FCSTD DOCUMENT  (FreeCAD 0.20R29603 (Git))
Label: equations_for_path_planning
License: All rights reserved
LicenseURL: http://en.wikipedia.org/wiki/All_rights_reserved
objects: Sketcher::SketchObject×12, PartDesign::Body×1, Spreadsheet::Sheet×1
note: 13 computed .brp shape members not serialized (recipe doc carries the construction recipe); baked Part::Feature solids carry a one-line shape summary decoded from their .brp

FEATURE [Sketcher::SketchObject] Sketch
  FullyConstrained = false
  MapMode = 5
  Support = -> [XY_Plane]
  sketch-geometry (40):
    g0: LineSegment StartX=13.0972 StartY=-137.963 StartZ=0 EndX=-119.149 EndY=-55.8265 EndZ=0
    g1: LineSegment StartX=-269.166 StartY=-4.11362 StartZ=0 EndX=-150.287 EndY=7.10111 EndZ=0
    g2: ArcOfCircle CenterX=-148.129 CenterY=-15.7711 CenterZ=0 NormalX=0 NormalY=0 NormalZ=1 AngleXU=0 Radius=22.9737 StartAngle=5.81975 EndAngle=7.94804
    g3: ArcOfCircle CenterX=-107.028 CenterY=-36.3106 CenterZ=0 NormalX=0 NormalY=0 NormalZ=1 AngleXU=0 Radius=22.9737 StartAngle=2.67816 EndAngle=4.15661
    g4: LineSegment StartX=-150.287 StartY=7.10111 StartZ=0 EndX=-139.078 EndY=-111.715 EndZ=0
    g5: LineSegment StartX=-119.149 StartY=-55.8265 StartZ=0 EndX=-56.1834 EndY=45.5543 EndZ=0
    g6: LineSegment StartX=-148.129 StartY=-15.7711 StartZ=0 EndX=-107.028 EndY=-36.3106 EndZ=0
    g7: LineSegment StartX=-150.287 StartY=7.10111 StartZ=0 EndX=-127.579 EndY=-26.0408 EndZ=0
    g8: LineSegment StartX=-119.149 StartY=-55.8265 StartZ=0 EndX=-127.579 EndY=-26.0408 EndZ=0
    g9: LineSegment StartX=-150.287 StartY=7.10111 StartZ=0 EndX=-119.149 EndY=-55.8265 EndZ=0
    g10: LineSegment StartX=222.705 StartY=-185.342 StartZ=0 EndX=152.096 EndY=-113.138 EndZ=0
    g11: LineSegment StartX=216.262 StartY=-75.3845 StartZ=0 EndX=305.183 EndY=-104.559 EndZ=0
    g12: Circle CenterX=209.656 CenterY=-95.5193 CenterZ=0 NormalX=0 NormalY=0 NormalZ=1 AngleXU=0 Radius=21.1908
    g13: Circle CenterX=136.945 CenterY=-127.954 CenterZ=0 NormalX=0 NormalY=0 NormalZ=1 AngleXU=0 Radius=21.1908
    g14: Circle CenterX=225.656 CenterY=-46.7518 CenterZ=0 NormalX=0 NormalY=0 NormalZ=1 AngleXU=0 Radius=30.1345
    g15: Circle CenterX=167.246 CenterY=-98.3223 CenterZ=0 NormalX=0 NormalY=0 NormalZ=1 AngleXU=0 Radius=21.1908
    g16: LineSegment StartX=13.0972 StartY=-137.963 StartZ=0 EndX=-70.8222 EndY=-85.8418 EndZ=0
    g17: LineSegment StartX=254 StartY=400 StartZ=0 EndX=400 EndY=230 EndZ=0
    g18: LineSegment StartX=508 StartY=203.2 StartZ=0 EndX=660.4 EndY=152.4 EndZ=0
    g19: ArcOfCircle CenterX=-47.1456 CenterY=-154.019 CenterZ=0 NormalX=0 NormalY=0 NormalZ=1 AngleXU=0 Radius=589.415 StartAngle=0.890474 EndAngle=6.99278
    g20: ArcOfCircle CenterX=694.389 CenterY=762.368 CenterZ=0 NormalX=0 NormalY=0 NormalZ=1 AngleXU=0 Radius=589.415 StartAngle=4.03207 EndAngle=4.39064
    g21: LineSegment StartX=13 StartY=7.5 StartZ=0 EndX=18.8 EndY=6 EndZ=0
    g22: LineSegment StartX=19.7 StartY=3.8 StartZ=0 EndX=25.3 EndY=6.1 EndZ=0
    g23: LineSegment StartX=18.8 StartY=6 StartZ=0 EndX=24.3818 EndY=4.55644 EndZ=0
    g24: GeomPoint X=22.6391 Y=5.00713 Z=0
    g25: ArcOfCircle CenterX=456.112 CenterY=278.191 CenterZ=0 NormalX=0 NormalY=0 NormalZ=1 AngleXU=0 Radius=73.9658 StartAngle=3.85119 EndAngle=4.90624
    g26: ArcOfCircle CenterX=484.61 CenterY=133.03 CenterZ=0 NormalX=0 NormalY=0 NormalZ=1 AngleXU=0 Radius=73.9658 StartAngle=1.24905 EndAngle=1.76465
    g27: LineSegment StartX=508 StartY=203.2 StartZ=0 EndX=353.856 EndY=254.581 EndZ=0
    g28: ArcOfCircle CenterX=563.835 CenterY=370.705 CenterZ=0 NormalX=0 NormalY=0 NormalZ=1 AngleXU=0 Radius=215.963 StartAngle=4.19072 EndAngle=4.39064
    g29: LineSegment StartX=508 StartY=203.2 StartZ=0 EndX=719.847 EndY=838.742 EndZ=0
    g30: LineSegment StartX=495.542 StartY=165.825 StartZ=0 EndX=589.09 EndY=134.642 EndZ=0
    g31: LineSegment StartX=400 StartY=230 StartZ=0 EndX=989.421 EndY=736.208 EndZ=0
    g32: LineSegment StartX=1251.67 StartY=-863.247 StartZ=0 EndX=1878.41 EndY=-863.247 EndZ=0
    g33: LineSegment StartX=1978.41 StartY=-963.247 StartZ=0 EndX=3494.4 EndY=-963.247 EndZ=0
    g34: ArcOfCircle CenterX=1878.41 CenterY=-913.247 CenterZ=0 NormalX=0 NormalY=0 NormalZ=1 AngleXU=0 Radius=50 StartAngle=-9e-16 EndAngle=1.5708
    g35: ArcOfCircle CenterX=1978.41 CenterY=-913.247 CenterZ=0 NormalX=0 NormalY=0 NormalZ=1 AngleXU=0 Radius=50 StartAngle=3.14159 EndAngle=4.71239
    g36: LineSegment StartX=1878.41 StartY=-863.247 StartZ=0 EndX=1978.41 EndY=-963.247 EndZ=0
    g37: LineSegment StartX=1928.41 StartY=-280.356 StartZ=0 EndX=1928.41 EndY=-1546.14 EndZ=0
    g38: LineSegment StartX=1878.41 StartY=-863.247 StartZ=0 EndX=1878.41 EndY=-913.247 EndZ=0
    g39: LineSegment StartX=1878.41 StartY=-913.247 StartZ=0 EndX=1928.41 EndY=-913.247 EndZ=0
  constraints (118):
    c: Tangent(g2,g1)
    c: Coincident(g3,g2)
    c: Tangent(g0,g3)
    c: Tangent(g3,g2)
    c: Equal(g2,g3)
    c: Coincident(g2,g1)
    c: Coincident(g0,g3)
    c: PointOnObject(g4,g1)
    c: PointOnObject(g5,g0)
    c: Perpendicular(g4,g1)
    c: Perpendicular(g0,g5)
    c: Equal(g4,g5)
    c: PointOnObject(g3,g5)
    c: PointOnObject(g2,g4)
    c: Coincident(g6,g2)
    c: Coincident(g6,g3)
    c: Angle(g4,g6) = 1.0133
    c: Angle(g5,g6) = 1.66314
    c: Angle(g5,g4) = 0.649838
    c: Coincident(g7,g4)
    c: Coincident(g7,g2)
    c: Coincident(g8,g5)
    c: Coincident(g8,g7)
    c: Angle(g8,g7) = -2.81667
    c: Distance(g6,g4) = 22.9737
    c: Distance(g6,g7) = 22.9737
    c: Distance(g6,g7) = 22.9737
    c: Coincident(g9,g4)
    c: Coincident(g9,g5)
    c: Angle(g4,g6) = 1.0133
    c: DistanceX(g1) = -269.166
    c: DistanceY(g1) = -4.11362
    c: Tangent(g12,g11)
    c: PointOnObject(g11,g12)
    c: DistanceX(g11) = 216.262
    c: DistanceY(g11) = -75.3845
    c: DistanceX(g11) = 305.183
    c: DistanceY(g11) = -104.559
    c: DistanceX(g10) = 222.705
    c: DistanceY(g10) = -185.342
    c: DistanceX(g10) = 152.096
    c: DistanceY(g10) = -113.138
    c: PointOnObject(g10,g13)
    c: Tangent(g10,g13)
    c: PointOnObject(g11,g14)
    c: Tangent(g14,g11)
    c: PointOnObject(g10,g15)
    c: Tangent(g15,g10)
    c: Equal(g12,g13)
    c: Coincident(g16,g0)
    c: PointOnObject(g5,g16)
    c: DistanceX(g16) = -70.8222
    c: DistanceY(g16) = -85.8418
    c: DistanceX(g16) = 13.0972
    c: DistanceY(g16) = -137.963
    c: Equal(g12,g15)
    c: Coincident(g20,g19)
    c: Coincident(g20,g18)
    c: Tangent(g20,g19)
    c: Tangent(g20,g18)
    c: DistanceX(g18) = 508
    c: DistanceY(g18) = 203.2
    c: DistanceX(g18) = 660.4
    c: DistanceX(g17) = 254
    c: DistanceY(g17) = 400
    c: DistanceY(g18) = 152.4
    c: DistanceY(g17) = 230
    c: Tangent(g17,g19) = 1.5708
    c: DistanceX(g-1,g17) = 400
    c: Equal(g19,g20)
    c: DistanceX(g21) = 13
    c: DistanceY(g21) = 7.5
    c: DistanceX(g21) = 18.8
    c: DistanceY(g21) = 6
    c: DistanceX(g22) = 19.7
    c: DistanceY(g22) = 3.8
    c: DistanceX(g22) = 25.3
    c: DistanceY(g22) = 6.1
    c: Coincident(g23,g21)
    c: Parallel(g21,g23)
    c: PointOnObject(g24,g23)
    c: PointOnObject(g24,g22)
    c: Tangent(g26,g25) = 1.5708
    c: Tangent(g25,g17) = -1.5708
    c: Tangent(g26,g18) = 1.5708
    c: Equal(g26,g25)
    c: Coincident(g27,g18)
    c: Parallel(g27,g18)
    c: PointOnObject(g17,g28)
    c: Tangent(g28,g17,g17) = -1.5708
    c: Coincident(g29,g18)
    c: Perpendicular(g18,g29)
    c: PointOnObject(g30,g29)
    c: Parallel(g30,g18)
    c: Tangent(g28,g30) = -1.5708
    c: Coincident(g31,g17)
    c: Perpendicular(g17,g31)
    c: Horizontal(g32)
    c: Horizontal(g33)
    c: Equal(g34,g35)
    c: Tangent(g35,g34) = 1.5708
    c: Tangent(g34,g32) = 1.5708
    c: Tangent(g35,g33) = -1.5708
    c: DistanceX(g32) = 1878.41
    c: DistanceY(g32) = -863.247
    c: Coincident(g36,g32)
    c: Coincident(g36,g33)
    c: Symmetric(g37,g37,g34)
    c: Tangent(g34,g37)
    c: Coincident(g38,g32)
    c: Coincident(g38,g34)
    c: Coincident(g39,g34)
    c: Coincident(g39,g34)
    c: Angle(g38,g36) = 0.785398
    c: Angle(g36,g39) = 0.785398
    c: DistanceX(g32,g33) = 100
    c: DistanceY(g32,g33) = -100
    c: Radius(g34) = 50
FEATURE [PartDesign::Body] Body
  Group = -> [Sketch]
  Origin = -> Origin
FEATURE [Spreadsheet::Sheet] Spreadsheet
FEATURE [Sketcher::SketchObject] Sketch001
  FullyConstrained = false
  MapMode = 2
  Support = -> [Sketch]
  sketch-geometry (6):
    g0: LineSegment StartX=9.98353 StartY=1.48336 StartZ=0 EndX=6.28174 EndY=10.773 EndZ=0
    g1: LineSegment StartX=10 StartY=12.4834 StartZ=0 EndX=10 EndY=2.48336 EndZ=0
    g2: ArcOfCircle CenterX=10.9586 CenterY=1.8719 CenterZ=0 NormalX=0 NormalY=0 NormalZ=1 AngleXU=0 Radius=1.04959 StartAngle=2.84602 EndAngle=3.5208
    g3: ArcOfCircle CenterX=8.95041 CenterY=2.48336 CenterZ=0 NormalX=0 NormalY=0 NormalZ=1 AngleXU=0 Radius=1.04959 StartAngle=5.98761 EndAngle=6.28319
    g4: LineSegment StartX=10 StartY=2.48336 StartZ=0 EndX=12.8335 EndY=2.48336 EndZ=0
    g5: LineSegment StartX=9.98353 StartY=1.48336 StartZ=0 EndX=12.493 EndY=2.48336 EndZ=0
  constraints (20):
    c: DistanceX(g0) = 9.98353
    c: DistanceY(g0) = 1.48336
    c: DistanceX(g0) = 6.28174
    c: DistanceY(g0) = 10.773
    c: DistanceX(g1) = 10
    c: DistanceY(g1) = 2.48336
    c: DistanceX(g1) = 10
    c: DistanceY(g1) = 12.4834
    c: Equal(g3,g2)
    c: Tangent(g3,g2) = 1.5708
    c: Tangent(g3,g1) = 1.5708
    c: Tangent(g2,g0) = 1.5708
    c: Radius(g2) = 1.04959
    c: Coincident(g4,g1)
    c: Perpendicular(g1,g4)
    c: Coincident(g5,g0)
    c: Perpendicular(g5,g0)
    c: PointOnObject(g5,g4)
    c: Distance(g5) = 2.70139
    c: Distance(g5,g1) = 2.49302
FEATURE [Sketcher::SketchObject] Sketch002
  FullyConstrained = false
  MapMode = 2
  Support = -> [Sketch001]
  sketch-geometry (6):
    g0: LineSegment StartX=17.549 StartY=7.05168 StartZ=0 EndX=10.2321 EndY=0.235299 EndZ=0
    g1: LineSegment StartX=10 StartY=11.2353 StartZ=0 EndX=10 EndY=1.2353 EndZ=0
    g2: ArcOfCircle CenterX=9.94609 CenterY=0.542355 CenterZ=0 NormalX=0 NormalY=0 NormalZ=1 AngleXU=0 Radius=0.419654 StartAngle=5.46239 EndAngle=7.25447
    g3: ArcOfCircle CenterX=10.4197 CenterY=1.2353 CenterZ=0 NormalX=0 NormalY=0 NormalZ=1 AngleXU=0 Radius=0.419654 StartAngle=3.14159 EndAngle=4.11288
    g4: LineSegment StartX=10 StartY=1.2353 StartZ=0 EndX=8.89489 EndY=1.2353 EndZ=0
    g5: LineSegment StartX=10.2321 StartY=0.235299 StartZ=0 EndX=9.30054 EndY=1.2353 EndZ=0
  constraints (17):
    c: DistanceX(g0) = 10.2321
    c: DistanceY(g0) = 0.235299
    c: DistanceX(g0) = 17.549
    c: DistanceY(g0) = 7.05168
    c: DistanceX(g1) = 10
    c: DistanceY(g1) = 1.2353
    c: DistanceX(g1) = 10
    c: DistanceY(g1) = 11.2353
    c: Equal(g3,g2)
    c: Tangent(g3,g2) = 1.5708
    c: Tangent(g3,g1) = -1.5708
    c: Tangent(g2,g0) = 1.5708
    c: Coincident(g4,g1)
    c: Perpendicular(g1,g4)
    c: Coincident(g5,g0)
    c: Perpendicular(g0,g5)
    c: PointOnObject(g5,g4)
FEATURE [Sketcher::SketchObject] Sketch003
  FullyConstrained = false
  MapMode = 2
  Support = -> [Sketch002]
  sketch-geometry (6):
    g0: LineSegment StartX=19.1 StartY=-1.7e-05 StartZ=0 EndX=9.1 EndY=6e-06 EndZ=0
    g1: LineSegment StartX=10 StartY=11 StartZ=0 EndX=10 EndY=1.00001 EndZ=0
    g2: ArcOfCircle CenterX=9.1 CenterY=0.902632 CenterZ=0 NormalX=0 NormalY=0 NormalZ=1 AngleXU=0 Radius=0.902626 StartAngle=4.71239 EndAngle=6.33715
    g3: ArcOfCircle CenterX=10.9026 CenterY=1.00001 CenterZ=0 NormalX=0 NormalY=0 NormalZ=1 AngleXU=0 Radius=0.902626 StartAngle=3.14159 EndAngle=3.19556
    g4: LineSegment StartX=10 StartY=1.00001 StartZ=0 EndX=6.80497 EndY=1.00001 EndZ=0
    g5: LineSegment StartX=9.1 StartY=6e-06 StartZ=0 EndX=9.1 EndY=1.00001 EndZ=0
  constraints (18):
    c: DistanceX(g0) = 9.1
    c: DistanceY(g0) = 6e-06
    c: DistanceX(g0) = 19.1
    c: DistanceY(g0) = -1.7e-05
    c: DistanceX(g1) = 10
    c: DistanceY(g1) = 1.00001
    c: DistanceX(g1) = 10
    c: DistanceY(g1) = 11
    c: Equal(g3,g2)
    c: Tangent(g2,g0) = 1.5708
    c: Tangent(g3,g2) = 1.5708
    c: Tangent(g3,g1) = -1.5708
    c: Coincident(g4,g1)
    c: Perpendicular(g1,g4)
    c: Coincident(g5,g0)
    c: Perpendicular(g0,g5)
    c: PointOnObject(g5,g4)
    c: Radius(g2) = 0.902626
FEATURE [Sketcher::SketchObject] Sketch004  label="Sketch005"
  FullyConstrained = false
  MapMode = 2
  Support = -> [Sketch003]
  sketch-geometry (6):
    g0: LineSegment StartX=2.77553 StartY=0.601402 StartZ=0 EndX=12.0482 EndY=4.34534 EndZ=0
    g1: LineSegment StartX=3.68106 StartY=1.06897 StartZ=0 EndX=13.2843 EndY=3.85774 EndZ=0
    g2: ArcOfCircle CenterX=2.12717 CenterY=2.2072 CenterZ=0 NormalX=0 NormalY=0 NormalZ=1 AngleXU=0 Radius=1.73175 StartAngle=5.09613 EndAngle=5.34108
    g3: ArcOfCircle CenterX=4.164 CenterY=-0.594071 CenterZ=0 NormalX=0 NormalY=0 NormalZ=1 AngleXU=0 Radius=1.73175 StartAngle=1.85342 EndAngle=2.19949
    g4: LineSegment StartX=2.77553 StartY=0.601402 StartZ=0 EndX=7.06476 EndY=-10.0218 EndZ=0
    g5: LineSegment StartX=3.68106 StartY=1.06897 StartZ=0 EndX=6.48437 EndY=-8.58438 EndZ=0
  constraints (17):
    c: DistanceX(g0) = 2.77553
    c: DistanceY(g0) = 0.601402
    c: DistanceX(g0) = 12.0482
    c: DistanceY(g0) = 4.34534
    c: DistanceX(g1) = 3.68106
    c: DistanceY(g1) = 1.06897
    c: DistanceX(g1) = 13.2843
    c: DistanceY(g1) = 3.85774
    c: Equal(g2,g3)
    c: Tangent(g2,g0) = -1.5708
    c: Tangent(g3,g2) = 1.5708
    c: Tangent(g3,g1) = 1.5708
    c: Coincident(g4,g0)
    c: Coincident(g5,g1)
    c: Perpendicular(g4,g0)
    c: Perpendicular(g1,g5)
    c: PointOnObject(g5,g4)
FEATURE [Sketcher::SketchObject] Sketch005  label="Sketch004"
  FullyConstrained = true
  MapMode = 2
  Support = -> [Sketch004]
  sketch-geometry (6):
    g0: LineSegment StartX=1.04064 StartY=0.1918 StartZ=0 EndX=10.5806 EndY=3.18995 EndZ=0
    g1: LineSegment StartX=1.9714 StartY=0.572491 StartZ=0 EndX=11.5747 EndY=3.36126 EndZ=0
    g2: LineSegment StartX=1.9714 StartY=0.572491 StartZ=0 EndX=14.748 EndY=-43.4243 EndZ=0
    g3: LineSegment StartX=1.04064 StartY=0.1918 StartZ=0 EndX=14.748 EndY=-43.4243 EndZ=0
    g4: ArcOfCircle CenterX=0.246036 CenterY=2.7202 CenterZ=0 NormalX=0 NormalY=0 NormalZ=1 AngleXU=0 Radius=2.65032 StartAngle=5.01689 EndAngle=5.19596
    g5: ArcOfCircle CenterX=2.71051 CenterY=-1.97268 CenterZ=0 NormalX=0 NormalY=0 NormalZ=1 AngleXU=0 Radius=2.65032 StartAngle=1.85342 EndAngle=2.05436
  constraints (17):
    c: DistanceX(g0) = 1.04064
    c: DistanceY(g0) = 0.1918
    c: DistanceX(g0) = 10.5806
    c: DistanceY(g0) = 3.18995
    c: DistanceX(g1) = 1.9714
    c: DistanceY(g1) = 0.572491
    c: DistanceX(g1) = 11.5747
    c: DistanceY(g1) = 3.36126
    c: Coincident(g2,g1)
    c: Coincident(g3,g0)
    c: Perpendicular(g3,g0)
    c: Perpendicular(g2,g1)
    c: Coincident(g3,g2)
    c: Equal(g4,g5)
    c: Tangent(g4,g0) = -1.5708
    c: Tangent(g5,g1) = 1.5708
    c: Tangent(g5,g4) = 1.5708
FEATURE [Sketcher::SketchObject] Sketch006
  FullyConstrained = true
  MapMode = 2
  Support = -> [Sketch003]
  sketch-geometry (6):
    g0: LineSegment StartX=36.4924 StartY=-40.865 StartZ=0 EndX=26.7052 EndY=-38.8135 EndZ=0
    g1: LineSegment StartX=10.7423 StartY=-4.56292 StartZ=0 EndX=18.021 EndY=2.29423 EndZ=0
    g2: ArcOfCircle CenterX=28.7839 CenterY=-28.8966 CenterZ=0 NormalX=0 NormalY=0 NormalZ=1 AngleXU=0 Radius=10.1324 StartAngle=4.50576 EndAngle=8.43328
    g3: ArcOfCircle CenterX=17.6902 CenterY=-11.938 CenterZ=0 NormalX=0 NormalY=0 NormalZ=1 AngleXU=0 Radius=10.1324 StartAngle=2.32638 EndAngle=5.29169
    g4: LineSegment StartX=10.7423 StartY=-4.56292 StartZ=0 EndX=29.6726 EndY=-24.657 EndZ=0
    g5: LineSegment StartX=26.7052 StartY=-38.8135 StartZ=0 EndX=29.6726 EndY=-24.657 EndZ=0
  constraints (17):
    c: DistanceX(g0) = 26.7052
    c: DistanceY(g0) = -38.8135
    c: DistanceX(g0) = 36.4924
    c: DistanceY(g0) = -40.865
    c: DistanceX(g1) = 10.7423
    c: DistanceY(g1) = -4.56292
    c: DistanceX(g1) = 18.021
    c: DistanceY(g1) = 2.29423
    c: Tangent(g3,g2) = 1.5708
    c: Tangent(g2,g0) = 1.5708
    c: Tangent(g3,g1) = 1.5708
    c: Equal(g3,g2)
    c: Coincident(g4,g1)
    c: Coincident(g5,g0)
    c: Perpendicular(g0,g5)
    c: Perpendicular(g1,g4)
    c: Coincident(g4,g5)
FEATURE [Sketcher::SketchObject] Sketch007
  FullyConstrained = true
  MapMode = 2
  Support = -> [Sketch006]
  sketch-geometry (6):
    g0: LineSegment StartX=0.978822 StartY=-0.181722 StartZ=0 EndX=10.7075 EndY=-2.49525 EndZ=0
    g1: LineSegment StartX=1.9519 StartY=-0.413561 StartZ=0 EndX=11.7347 EndY=-2.48631 EndZ=0
    g2: LineSegment StartX=0.978822 StartY=-0.181722 StartZ=0 EndX=10.3538 EndY=39.2411 EndZ=0
    g3: LineSegment StartX=1.9519 StartY=-0.413561 StartZ=0 EndX=10.3538 EndY=39.2411 EndZ=0
    g4: ArcOfCircle CenterX=-2.81305 CenterY=-16.127 CenterZ=0 NormalX=0 NormalY=0 NormalZ=1 AngleXU=0 Radius=16.39 StartAngle=1.31915 EndAngle=1.33733
    g5: ArcOfCircle CenterX=5.34912 CenterY=15.6205 CenterZ=0 NormalX=0 NormalY=0 NormalZ=1 AngleXU=0 Radius=16.39 StartAngle=4.46074 EndAngle=4.5036
  constraints (17):
    c: DistanceX(g0) = 0.978822
    c: DistanceY(g0) = -0.181722
    c: DistanceX(g0) = 10.7075
    c: DistanceY(g0) = -2.49525
    c: DistanceX(g1) = 1.9519
    c: DistanceY(g1) = -0.413561
    c: DistanceX(g1) = 11.7347
    c: DistanceY(g1) = -2.48631
    c: Coincident(g2,g0)
    c: Coincident(g3,g1)
    c: Perpendicular(g1,g3)
    c: Perpendicular(g0,g2)
    c: Coincident(g2,g3)
    c: Equal(g4,g5)
    c: Tangent(g5,g4) = 1.5708
    c: Tangent(g4,g0) = 1.5708
    c: Tangent(g5,g1) = -1.5708
FEATURE [Sketcher::SketchObject] Sketch008
  FullyConstrained = true
  MapMode = 2
  Support = -> [Sketch007]
  sketch-geometry (4):
    g0: LineSegment StartX=2.37421 StartY=7.41429 StartZ=0 EndX=11.2171 EndY=12.0838 EndZ=0
    g1: LineSegment StartX=3.25845 StartY=7.8814 StartZ=0 EndX=12.0583 EndY=12.6314 EndZ=0
    g2: ArcOfCircle CenterX=24.1215 CenterY=-33.7699 CenterZ=0 NormalX=0 NormalY=0 NormalZ=1 AngleXU=0 Radius=46.5734 StartAngle=2.05046 EndAngle=2.05663
    g3: ArcOfCircle CenterX=-18.8637 CenterY=48.8654 CenterZ=0 NormalX=0 NormalY=0 NormalZ=1 AngleXU=0 Radius=46.5734 StartAngle=5.19205 EndAngle=5.20735
  constraints (12):
    c: DistanceX(g0) = 2.37421
    c: DistanceY(g0) = 7.41429
    c: DistanceX(g0) = 11.2171
    c: DistanceY(g0) = 12.0838
    c: DistanceX(g1) = 3.25845
    c: DistanceY(g1) = 7.8814
    c: DistanceX(g1) = 12.0583
    c: DistanceY(g1) = 12.6314
    c: Tangent(g3,g2) = 1.5708
    c: Tangent(g2,g0) = 1.5708
    c: Tangent(g3,g1) = -1.5708
    c: Equal(g2,g3)
FEATURE [Sketcher::SketchObject] Sketch009
  FullyConstrained = false
  MapMode = 2
  Support = -> [Sketch008]
  sketch-geometry (11):
    g0: LineSegment StartX=1 StartY=1 StartZ=0 EndX=2 EndY=2 EndZ=0
    g1: GeomPoint X=9.77368e+06 Y=-1.21619e+07 Z=0
    g2: LineSegment StartX=0.8 StartY=0.5 StartZ=0 EndX=0.595103 EndY=0.321908 EndZ=0
    g3: ArcOfCircle CenterX=1.19663 CenterY=0.803369 CenterZ=0 NormalX=0 NormalY=0 NormalZ=1 AngleXU=0 Radius=0.278078 StartAngle=4.31701 EndAngle=8.63938
    g4: ArcOfCircle CenterX=0.982423 CenterY=0.290121 CenterZ=0 NormalX=0 NormalY=0 NormalZ=1 AngleXU=0 Radius=0.278078 StartAngle=1.17542 EndAngle=2.28632
    g5: ArcOfCircle CenterX=0.815419 CenterY=1.18458 CenterZ=0 NormalX=0 NormalY=0 NormalZ=1 AngleXU=0 Radius=0.261037 StartAngle=5.49779 EndAngle=10.6299
    g6: ArcOfCircle CenterX=0.628757 CenterY=0.697018 CenterZ=0 NormalX=0 NormalY=0 NormalZ=1 AngleXU=0 Radius=0.261037 StartAngle=5.42791 EndAngle=7.48835
    g7: LineSegment StartX=1 StartY=1 StartZ=0 EndX=1.19663 EndY=0.803369 EndZ=0
    g8: LineSegment StartX=0.8 StartY=0.5 StartZ=0 EndX=0.982423 EndY=0.290121 EndZ=0
    g9: LineSegment StartX=1 StartY=1 StartZ=0 EndX=0.815419 EndY=1.18458 EndZ=0
    g10: LineSegment StartX=0.628757 StartY=0.697018 StartZ=0 EndX=0.8 EndY=0.5 EndZ=0
  constraints (22):
    c: DistanceX(g0) = 1
    c: DistanceY(g0) = 1
    c: DistanceX(g0) = 2
    c: DistanceY(g0) = 2
    c: Tangent(g3,g0) = 1.5708
    c: Tangent(g4,g2) = -1.5708
    c: Tangent(g4,g3) = 1.5708
    c: Equal(g5,g6)
    c: Tangent(g6,g2) = 1.5708
    c: Tangent(g5,g0) = -1.5708
    c: Tangent(g6,g5) = 1.5708
    c: Coincident(g7,g0)
    c: Coincident(g7,g3)
    c: Coincident(g8,g2)
    c: Coincident(g8,g4)
    c: Coincident(g9,g0)
    c: Coincident(g9,g5)
    c: Coincident(g10,g6)
    c: Coincident(g10,g2)
    c: DistanceX(g2) = 0.8
    c: DistanceY(g2) = 0.5
    c: Equal(g4,g3)
FEATURE [Sketcher::SketchObject] Sketch010
  FullyConstrained = false
  MapMode = 2
  Support = -> [Sketch009]
  sketch-geometry (7):
    g0: LineSegment StartX=6.98834 StartY=12.2806 StartZ=0 EndX=1.64979 EndY=20.7363 EndZ=0
    g1: LineSegment StartX=0.76254 StartY=21.3513 StartZ=0 EndX=6.27273 EndY=13.0064 EndZ=0
    g2: ArcOfCircle CenterX=5.93027 CenterY=11.6126 CenterZ=0 NormalX=0 NormalY=0 NormalZ=1 AngleXU=0 Radius=1.2513 StartAngle=0.563153 EndAngle=0.983531
    g3: ArcOfCircle CenterX=7.31693 CenterY=13.6959 CenterZ=0 NormalX=0 NormalY=0 NormalZ=1 AngleXU=0 Radius=1.2513 StartAngle=3.72518 EndAngle=4.12512
    g4: ArcOfCircle CenterX=1.04731e+06 CenterY=661229 CenterZ=0 NormalX=0 NormalY=0 NormalZ=1 AngleXU=0 Radius=1.23857e+06 StartAngle=3.70516 EndAngle=9.98793
    g5: ArcOfCircle CenterX=-1.04674e+06 CenterY=-662080 CenterZ=0 NormalX=0 NormalY=0 NormalZ=1 AngleXU=0 Radius=1.23857e+06 StartAngle=0.563572 EndAngle=0.563991
    g6: LineSegment StartX=3.62319 StartY=17.019 StartZ=0 EndX=129.774 EndY=-211.32 EndZ=0
  constraints (18):
    c: DistanceX(g0) = 1.64979
    c: DistanceY(g0) = 20.7363
    c: DistanceX(g0) = 6.98834
    c: DistanceY(g0) = 12.2806
    c: DistanceX(g1) = 6.27273
    c: DistanceY(g1) = 13.0064
    c: DistanceX(g1) = 0.76254
    c: DistanceY(g1) = 21.3513
    c: Tangent(g3,g2) = 1.5708
    c: Tangent(g2,g0) = -1.5708
    c: Tangent(g3,g1) = -1.5708
    c: Equal(g3,g2)
    c: Coincident(g5,g1)
    c: Tangent(g4,g0) = 1.5708
    c: Equal(g5,g4)
    c: Tangent(g5,g4) = 1.5708
    c: PointOnObject(g6,g1)
    c: PointOnObject(g1,g6)
FEATURE [Sketcher::SketchObject] Sketch011
  FullyConstrained = false
  MapMode = 2
  Support = -> [Sketch010]
  sketch-geometry (8):
    g0: LineSegment StartX=-51.5151 StartY=-13.1655 StartZ=0 EndX=-70.4763 EndY=-6.80367 EndZ=0
    g1: LineSegment StartX=1.34304 StartY=15.1769 StartZ=0 EndX=-1.44 EndY=-4.6281 EndZ=0
    g2: LineSegment StartX=-51.5151 StartY=-13.1655 StartZ=0 EndX=-49.6366 EndY=-7.56662 EndZ=0
    g3: LineSegment StartX=-1.44 StartY=-4.6281 StartZ=0 EndX=12.9996 EndY=-6.65718 EndZ=0
    g4: ArcOfCircle CenterX=-46.678 CenterY=1.25123 CenterZ=0 NormalX=0 NormalY=0 NormalZ=1 AngleXU=0 Radius=15.2066 StartAngle=6.15913 EndAngle=10.6719
    g5: ArcOfCircle CenterX=-16.4986 CenterY=-2.51204 CenterZ=0 NormalX=0 NormalY=0 NormalZ=1 AngleXU=0 Radius=15.2066 StartAngle=3.01754 EndAngle=6.14358
    g6: ArcOfCircle CenterX=-84.5515 CenterY=-111.629 CenterZ=0 NormalX=0 NormalY=0 NormalZ=1 AngleXU=0 Radius=103.858 StartAngle=1.24708 EndAngle=6.74498
    g7: ArcOfCircle CenterX=101.408 CenterY=-19.0805 CenterZ=0 NormalX=0 NormalY=0 NormalZ=1 AngleXU=0 Radius=103.858 StartAngle=3.00198 EndAngle=3.60339
  constraints (20):
    c: DistanceX(g0) = -51.5151
    c: DistanceY(g0) = -13.1655
    c: DistanceX(g0) = -70.4763
    c: DistanceY(g0) = -6.80367
    c: DistanceX(g1) = -1.44
    c: DistanceY(g1) = -4.6281
    c: Coincident(g2,g0)
    c: Coincident(g3,g1)
    c: Perpendicular(g2,g0)
    c: Perpendicular(g1,g3)
    c: DistanceX(g1) = 1.34304
    c: DistanceY(g1) = 15.1769
    c: Tangent(g5,g1) = 1.5708
    c: Tangent(g4,g0) = 1.5708
    c: Equal(g4,g5)
    c: Tangent(g5,g4) = 1.5708
    c: Tangent(g6,g0) = -1.5708
    c: Tangent(g7,g1) = -1.5708
    c: Equal(g6,g7)
    c: Tangent(g7,g6) = 1.5708
